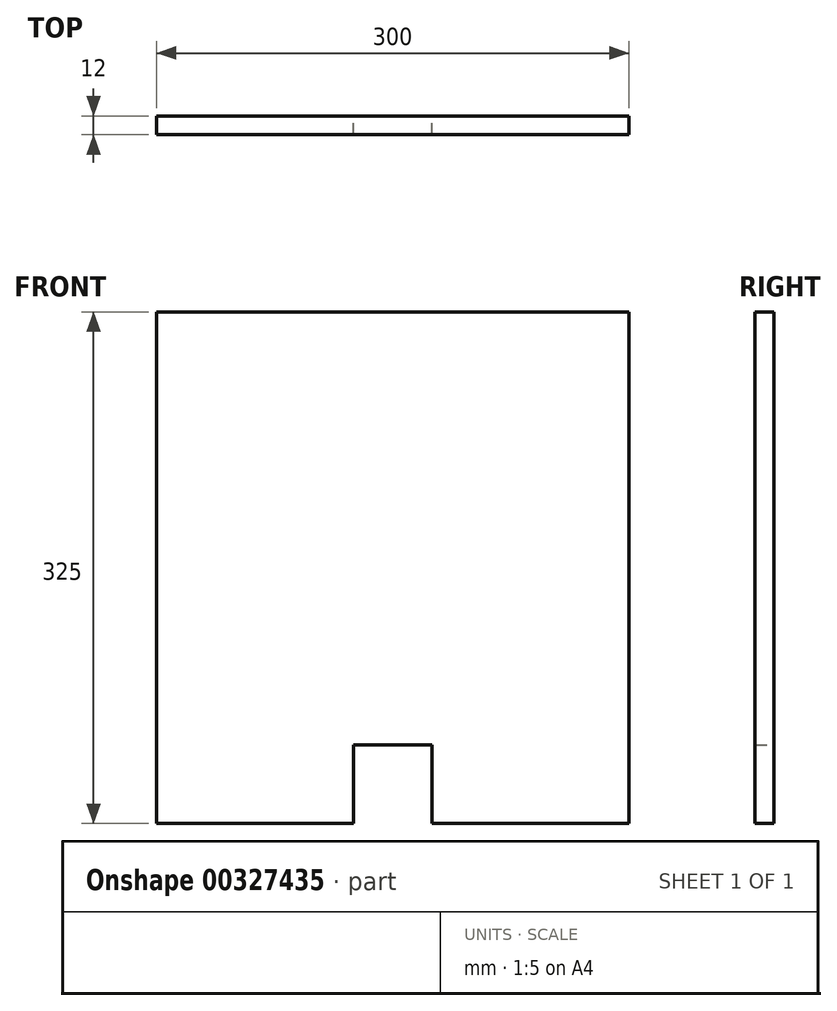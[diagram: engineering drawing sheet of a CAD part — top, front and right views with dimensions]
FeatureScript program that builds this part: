
annotation { "Feature Type Name" : "Feature", "Feature Type Description" : "" }
export const myFeature = defineFeature(function(context is Context, id is Id, definition is map)
    precondition{}
    {
        {
            var Q0;
            Q0=qCreatedBy(makeId("Front.planeOp"),FACE);
            var sketch = newSketch(context, id + "F0", { "sketchPlane" : qUnion([Q0])});
            skLineSegment(sketch, "E0", {"start": v(-202, -53.75) * mm, "end": v(-77, -53.75) * mm});
            skLineSegment(sketch, "E1", {"start": v(-77, -3.75) * mm, "end": v(-77, -53.75) * mm});
            skLineSegment(sketch, "E2", {"start": v(-27, -3.75) * mm, "end": v(-27, -53.75) * mm});
            skLineSegment(sketch, "E3", {"start": v(-77, -3.75) * mm, "end": v(-27, -3.75) * mm});
            skLineSegment(sketch, "E4.trimOffspring", {"start": v(-27, -53.75) * mm, "end": v(98, -53.75) * mm});
            skLineSegment(sketch, "E5", {"start": v(-202, -53.75) * mm, "end": v(-202, 271.25) * mm});
            skLineSegment(sketch, "E6", {"start": v(-202, 271.25) * mm, "end": v(98, 271.25) * mm});
            skLineSegment(sketch, "E7", {"start": v(98, 271.25) * mm, "end": v(98, -53.75) * mm});
            skSolve(sketch);
        }
        {
            var Q0;
            Q0=makeQuery(id+"F0.imprint","IMPRINT",FACE,{"disambiguationData":[TD([[makeQuery(id+"F0.imprint","IMPRINT",EDGE,{"derivedFrom":sQuery(id+"F0.wireOp",EDGE,"E0")}),1.0]])]});
            extrude(context, id + "F1", {"entities" : qUnion([Q0]), "depth" : 12 * mm});
        }
    });
